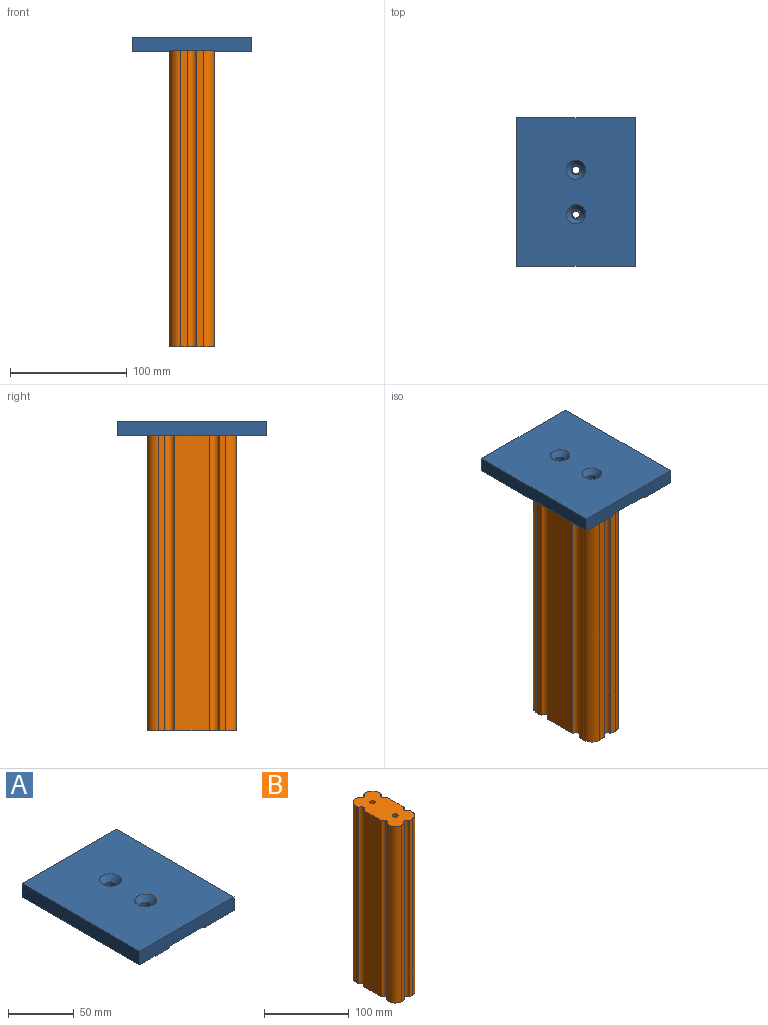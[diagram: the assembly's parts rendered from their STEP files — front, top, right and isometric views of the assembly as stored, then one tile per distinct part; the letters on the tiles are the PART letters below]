
ASSEMBLY  parts=2 mates=1
PART A: 14 faces, bbox 101.6x127x12.7 mm
  f0: plane 127x31.75mm, normal (0,0,-1), area 4032.3mm2, adj f1,f3,f4,f7
  f1: plane 101.6x12.7mm, normal (0,-1,0), area 1229.8mm2, adj f0,f2,f4,f5,f6,f7,f8,f9
  f2: plane 127x12.7mm, normal (1,0,0), area 1612.9mm2, adj f1,f3,f5,f6
  f3: plane 101.6x12.7mm, normal (0,1,0), area 1229.8mm2, adj f0,f2,f4,f5,f6,f7,f8,f9
  f4: plane 127x12.7mm, normal (-1,0,0), area 1612.9mm2, adj f0,f1,f3,f5
  f5: plane 127x101.6mm, normal (0,0,1), area 12467.1mm2, adj f1,f2,f3,f4,f11,f13
  f6: plane 127x31.75mm, normal (0,0,-1), area 4032.2mm2, adj f1,f2,f3,f8
  f7: plane 127x1.59mm, normal (1,0,0), area 201.6mm2, adj f0,f1,f3,f9
  f8: plane 127x1.59mm, normal (-1,0,0), area 201.6mm2, adj f1,f3,f6,f9
  f9: plane 127x38.1mm, normal (0,0,-1), area 4727mm2, adj f1,f3,f7,f8,f10,f12
  f10: cylinder r=4.22mm len=8.43mm, axis (0,0,1), area 169mm2, adj f9,f11
  f11: cone r=4.22mm half-angle=41deg, axis (0,0,1), area 247.2mm2, adj f5,f10
  f12: cylinder r=4.22mm len=8.43mm, axis (0,0,1), area 169mm2, adj f9,f13
  f13: cone r=4.22mm half-angle=41deg, axis (0,0,1), area 247.2mm2, adj f5,f12
PART B: 24 faces, bbox 38.1x76.2x254 mm
  f0: plane 254x29.72mm, normal (1,0,0), area 7548.4mm2, adj f9,f10,f13,f16
  f1: plane 254x5.33mm, normal (1,0,0), area 1354.8mm2, adj f9,f10,f16,f23
  f2: plane 254x5.33mm, normal (1,0,0), area 1354.8mm2, adj f9,f10,f13,f20
  f3: plane 254x5.33mm, normal (0,1,0), area 1354.8mm2, adj f9,f10,f17,f20
  f4: plane 254x29.72mm, normal (-1,0,0), area 7548.4mm2, adj f9,f10,f12,f14
  f5: plane 254x5.33mm, normal (-1,0,0), area 1354.8mm2, adj f9,f10,f14,f22
  f6: plane 254x5.33mm, normal (-1,0,0), area 1354.8mm2, adj f9,f10,f12,f21
  f7: plane 254x5.33mm, normal (0,-1,0), area 1354.8mm2, adj f9,f10,f15,f23
  f8: plane 254x5.33mm, normal (0,-1,0), area 1354.8mm2, adj f9,f10,f15,f22
  f9: plane 76.2x38.1mm, normal (0,0,1), area 2592.9mm2, adj f0,f1,f2,f3,f4,f5,f6,f7
  f10: plane 76.2x38.1mm, normal (0,0,-1), area 2592.9mm2, adj f0,f1,f2,f3,f4,f5,f6,f7
  f11: plane 254x5.33mm, normal (0,1,0), area 1354.8mm2, adj f9,f10,f17,f21
  f12: cylinder r=4.19mm len=254mm, axis (0,0,1), area 3344.3mm2, adj f4,f6,f9,f10
  f13: cylinder r=4.19mm len=254mm, axis (0,0,1), area 3344.3mm2, adj f0,f2,f9,f10
  f14: cylinder r=4.19mm len=254mm, axis (0,0,1), area 3344.3mm2, adj f4,f5,f9,f10
  f15: cylinder r=4.19mm len=254mm, axis (0,0,1), area 3344.3mm2, adj f7,f8,f9,f10
  f16: cylinder r=4.19mm len=254mm, axis (0,0,1), area 3344.3mm2, adj f0,f1,f9,f10
  f17: cylinder r=4.19mm len=254mm, axis (0,0,1), area 3344.3mm2, adj f3,f9,f10,f11
  f18: cylinder r=3.26mm len=254mm, axis (0,0,1), area 5209mm2, adj f9,f10
  f19: cylinder r=3.26mm len=254mm, axis (0,0,1), area 5209mm2, adj f9,f10
  f20: cylinder r=9.53mm len=254mm, axis (0,0,1), area 3800.3mm2, adj f2,f3,f9,f10
  f21: cylinder r=9.53mm len=254mm, axis (0,0,-1), area 3800.3mm2, adj f6,f9,f10,f11
  f22: cylinder r=9.53mm len=254mm, axis (0,0,1), area 3800.3mm2, adj f5,f8,f9,f10
  f23: cylinder r=9.53mm len=254mm, axis (0,0,-1), area 3800.3mm2, adj f1,f7,f9,f10
PLACE A t=(0,0,12.83)mm
PLACE B t=(0,0,-239.58)mm
MATE fastened B.f18 <-> A.f12  axis (0,0,1) through (0,-19.05,14.42)mm
